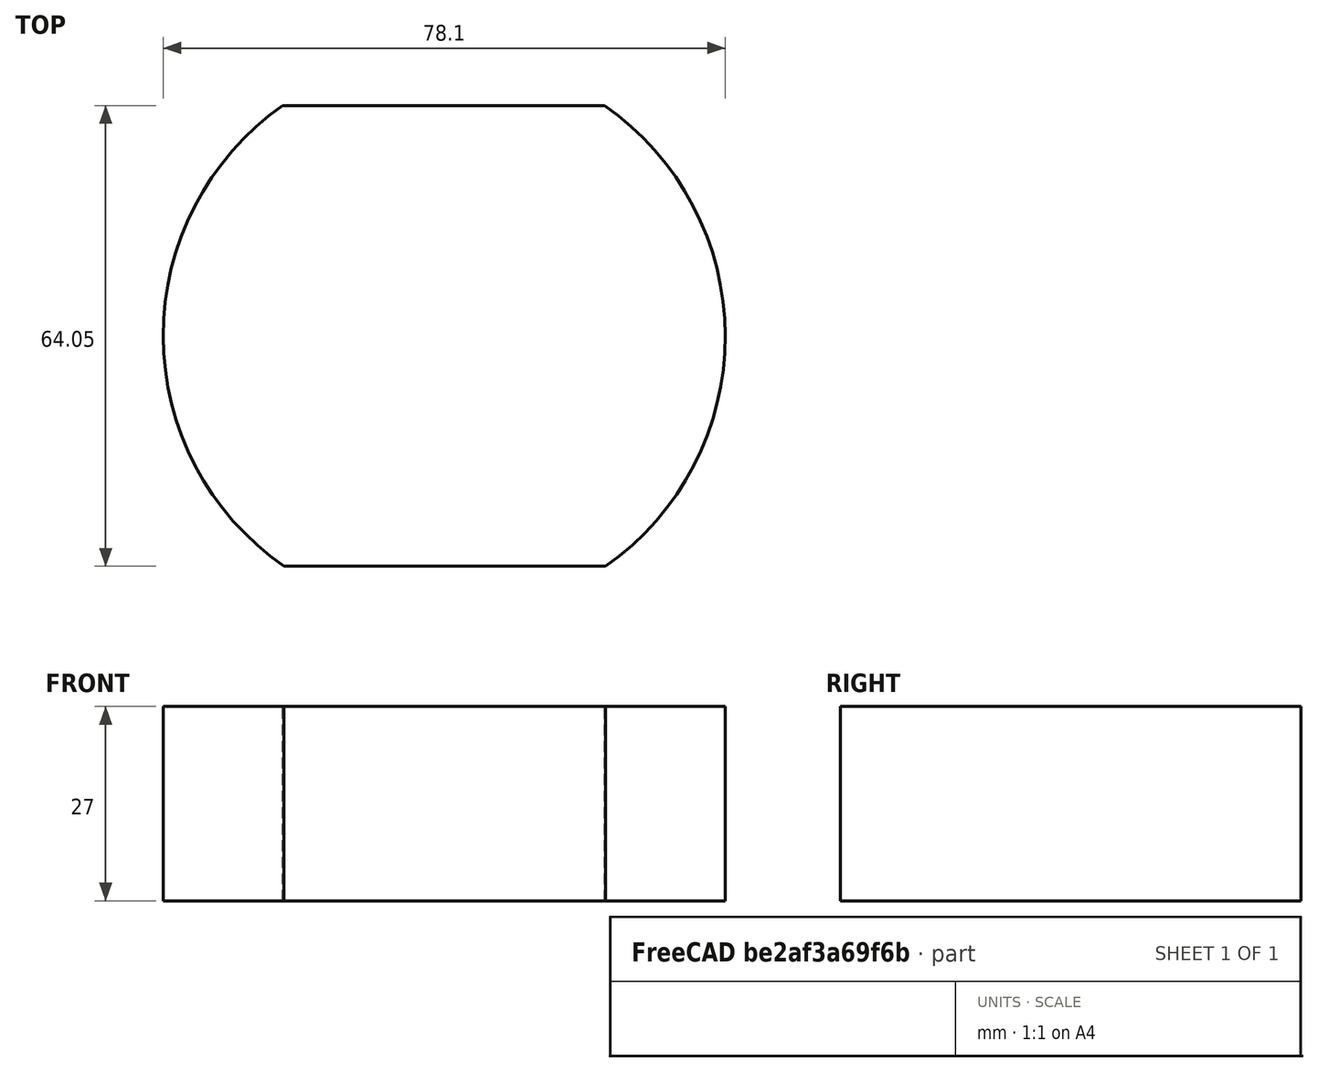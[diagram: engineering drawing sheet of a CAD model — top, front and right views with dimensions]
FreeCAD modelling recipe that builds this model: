
FCSTD DOCUMENT  (FreeCAD 1.0R39319 (Git))
Label: chapa_circle_90mm
License: All rights reserved
LicenseURL: https://en.wikipedia.org/wiki/All_rights_reserved
objects: Sketcher::SketchObject×1, PartDesign::Pad×1, PartDesign::Body×1
note: 6 computed .brp shape members not serialized (recipe doc carries the construction recipe); baked Part::Feature solids carry a one-line shape summary decoded from their .brp

FEATURE [Sketcher::SketchObject] Sketch_1
  ArcFitTolerance = 1e-06
  AttachmentSupport = -> [XY_Plane]
  FullyConstrained = false
  MakeInternals = false
  MapMode = 5
  sketch-geometry (4):
    g0: ArcOfCircle CenterX=-0.00137365 CenterY=6.61917 CenterZ=0 NormalX=0 NormalY=0 NormalZ=1 AngleXU=0 Radius=39.0547 StartAngle=5.32483 EndAngle=7.24741
    g1: LineSegment StartX=22.262 StartY=38.7067 StartZ=0 EndX=-22.4508 EndY=38.7067 EndZ=0
    g2: ArcOfCircle CenterX=0.00220858 CenterY=6.7507 CenterZ=0 NormalX=0 NormalY=0 NormalZ=1 AngleXU=0 Radius=39.0554 StartAngle=2.18328 EndAngle=4.1058
    g3: LineSegment StartX=-22.262 StartY=-25.3372 StartZ=0 EndX=22.4499 EndY=-25.3372 EndZ=0
  constraints (7):
    c: Coincident(g0,g1)
    c: Coincident(g1,g2)
    c: Coincident(g2,g3)
    c: Coincident(g3,g0)
    c: Parallel(g1,g3)
    c: Horizontal(g1)
    c: Distance(g1,g3) = 78
FEATURE [PartDesign::Pad] Pad_1
  Direction = (0,0,1)
  Length = 27
  Length2 = 10
  Profile = -> Sketch_1
  Refine = true
  Suppressed = false
  Type = 0
FEATURE [PartDesign::Body] Body
  AllowCompound = false
  Group = -> [Sketch_1,Pad_1]
  Origin = -> Origin
  Tip = -> Pad_1
